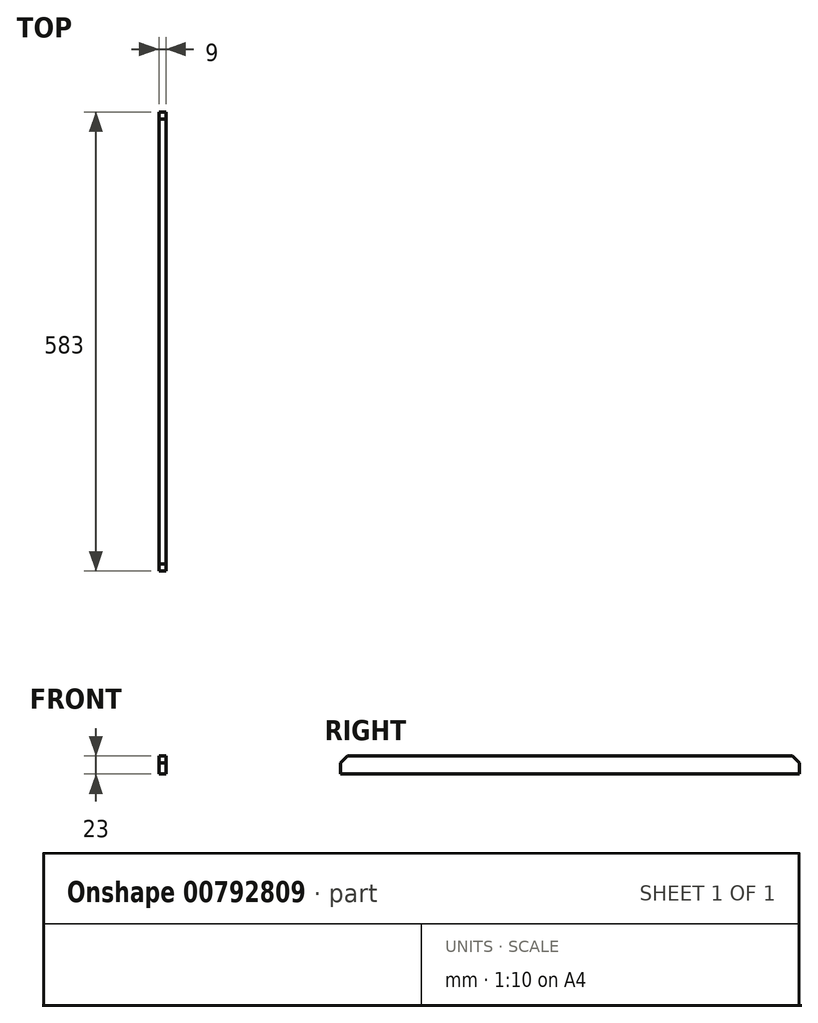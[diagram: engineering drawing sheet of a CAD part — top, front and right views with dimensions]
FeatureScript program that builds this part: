
annotation { "Feature Type Name" : "Feature", "Feature Type Description" : "" }
export const myFeature = defineFeature(function(context is Context, id is Id, definition is map)
    precondition{}
    {
        {
            var Q0;
            Q0=qCreatedBy(makeId("Right.planeOp"),FACE);
            var sketch = newSketch(context, id + "F0", { "sketchPlane" : qUnion([Q0])});
            skLineSegment(sketch, "E0.bottom", {"start": v(291.5, -11.5) * mm, "end": v(-291.5, -11.5) * mm});
            skLineSegment(sketch, "E0.top", {"start": v(291.5, 11.5) * mm, "end": v(-291.5, 11.5) * mm});
            skLineSegment(sketch, "E0.left", {"start": v(291.5, -11.5) * mm, "end": v(291.5, 11.5) * mm});
            skLineSegment(sketch, "E0.right", {"start": v(-291.5, -11.5) * mm, "end": v(-291.5, 11.5) * mm});
            skPoint(sketch, "E0.middle", {"position": v(0, 0) * mm});
            skSolve(sketch);
        }
        {
            var Q0;
            Q0 = qSketchRegion(id + "F0", true);
            extrude(context, id + "F1", {"entities" : qUnion([Q0]), "depth" : 9 * mm, "offsetDistance" : 25 * mm});
        }
        {
            var Q0;
            Q0=makeQuery(id+"F1.opExtrude","SWEPT_EDGE",EDGE,{"disambiguationData":[OSD([sQuery(id+"F0.wireOp",EDGE,"E0.top"),sQuery(id+"F0.wireOp",EDGE,"E0.left")])]});
            var Q1;
            Q1=makeQuery(id+"F1.opExtrude","SWEPT_EDGE",EDGE,{"disambiguationData":[OSD([sQuery(id+"F0.wireOp",EDGE,"E0.top"),sQuery(id+"F0.wireOp",EDGE,"E0.right")])]});
            chamfer(context, id + "F2", {"entities" : qUnion([Q0, Q1]), "width" : 9 * mm, "tangentPropagation" : true});
        }
    });
